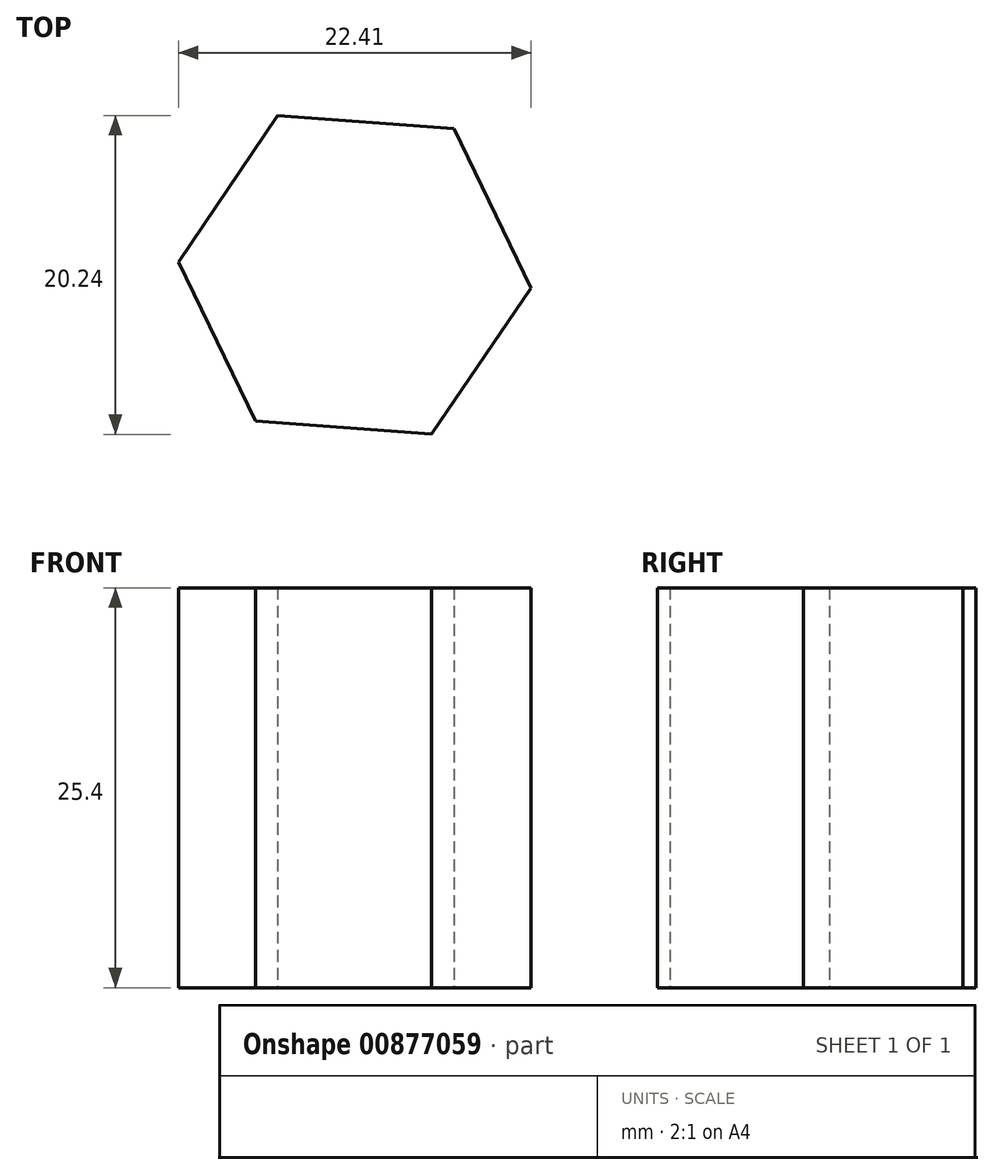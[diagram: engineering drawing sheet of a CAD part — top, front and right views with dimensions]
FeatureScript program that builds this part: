
annotation { "Feature Type Name" : "Feature", "Feature Type Description" : "" }
export const myFeature = defineFeature(function(context is Context, id is Id, definition is map)
    precondition{}
    {
        {
            var Q0;
            Q0=qCreatedBy(makeId("Top.planeOp"),FACE);
            var sketch = newSketch(context, id + "F0", { "sketchPlane" : qUnion([Q0])});
            skCircle(sketch, "E0", {"center": v(0, 0) * mm, "radius": 74.85 * mm});
            skCircle(sketch, "E1", {"center": v(0, 0) * mm, "radius": 15.5 * mm});
            skCircle(sketch, "E2.cCircle", {"center": v(0, 61.18) * mm, "radius": 10.9 * mm, "construction": true});
            skLineSegment(sketch, "E2.0", {"start": v(10.67, 54.49) * mm, "end": v(-0.45, 48.59) * mm});
            skLineSegment(sketch, "E2.1", {"start": v(-0.45, 48.59) * mm, "end": v(-11.13, 55.27) * mm});
            skLineSegment(sketch, "E2.2", {"start": v(-11.13, 55.27) * mm, "end": v(-10.67, 67.86) * mm});
            skLineSegment(sketch, "E2.3", {"start": v(-10.67, 67.86) * mm, "end": v(0.45, 73.76) * mm});
            skLineSegment(sketch, "E2.4", {"start": v(0.45, 73.76) * mm, "end": v(11.13, 67.08) * mm});
            skLineSegment(sketch, "E2.5", {"start": v(11.13, 67.08) * mm, "end": v(10.67, 54.49) * mm});
            skPoint(sketch, "E2.0.midPoint", {"position": v(5.11, 51.54) * mm});
            skCircle(sketch, "E3.cCircle", {"center": v(-60.3, 0) * mm, "radius": 10.8 * mm, "construction": true});
            skLineSegment(sketch, "E3.0", {"start": v(-54.07, 10.8) * mm, "end": v(-47.84, 0) * mm});
            skLineSegment(sketch, "E3.1", {"start": v(-47.84, 0) * mm, "end": v(-54.06, -10.79) * mm});
            skLineSegment(sketch, "E3.2", {"start": v(-54.06, -10.79) * mm, "end": v(-66.52, -10.8) * mm});
            skLineSegment(sketch, "E3.3", {"start": v(-66.52, -10.8) * mm, "end": v(-72.76, 0) * mm});
            skLineSegment(sketch, "E3.4", {"start": v(-72.76, 0) * mm, "end": v(-66.54, 10.79) * mm});
            skLineSegment(sketch, "E3.5", {"start": v(-66.54, 10.79) * mm, "end": v(-54.07, 10.8) * mm});
            skPoint(sketch, "E3.0.midPoint", {"position": v(-50.96, 5.4) * mm});
            skCircle(sketch, "E4.cCircle", {"center": v(0, -57.38) * mm, "radius": 10.77 * mm, "construction": true});
            skLineSegment(sketch, "E4.0", {"start": v(-0.75, -44.96) * mm, "end": v(10.38, -50.52) * mm});
            skLineSegment(sketch, "E4.1", {"start": v(10.38, -50.52) * mm, "end": v(11.13, -62.94) * mm});
            skLineSegment(sketch, "E4.2", {"start": v(11.13, -62.94) * mm, "end": v(0.75, -69.8) * mm});
            skLineSegment(sketch, "E4.3", {"start": v(0.75, -69.8) * mm, "end": v(-10.38, -64.23) * mm});
            skLineSegment(sketch, "E4.4", {"start": v(-10.38, -64.23) * mm, "end": v(-11.13, -51.82) * mm});
            skLineSegment(sketch, "E4.5", {"start": v(-11.13, -51.82) * mm, "end": v(-0.75, -44.96) * mm});
            skPoint(sketch, "E4.0.midPoint", {"position": v(4.82, -47.74) * mm});
            skLineSegment(sketch, "E5.0", {"start": v(50.19, -9.3) * mm, "end": v(45.3, 0.82) * mm});
            skLineSegment(sketch, "E5.1", {"start": v(45.3, 0.82) * mm, "end": v(51.61, 10.12) * mm});
            skLineSegment(sketch, "E5.2", {"start": v(51.61, 10.12) * mm, "end": v(62.82, 9.3) * mm});
            skLineSegment(sketch, "E5.3", {"start": v(62.82, 9.3) * mm, "end": v(67.7, -0.82) * mm});
            skLineSegment(sketch, "E5.4", {"start": v(67.7, -0.82) * mm, "end": v(61.4, -10.12) * mm});
            skLineSegment(sketch, "E5.5", {"start": v(61.4, -10.12) * mm, "end": v(50.19, -9.3) * mm});
            skPoint(sketch, "E5.0.midPoint", {"position": v(47.74, -4.23) * mm});
            skSolve(sketch);
        }
        {
            var Q0;
            Q0=makeQuery(id+"F0.imprint","IMPRINT",FACE,{"disambiguationData":[TD([[makeQuery(id+"F0.imprint","IMPRINT",EDGE,{"derivedFrom":sQuery(id+"F0.wireOp",EDGE,"E5.0")}),-1.0]])]});
            extrude(context, id + "F1", {"entities" : qUnion([Q0]), "depth" : 25.4 * mm, "offsetDistance" : 25.4 * mm});
        }
    });
